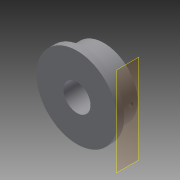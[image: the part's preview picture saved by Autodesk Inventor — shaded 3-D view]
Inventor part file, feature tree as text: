
AUTODESK INVENTOR PART (.ipt)
format: ipt  version: 2015 SP2 (Build 190223200, 223)  size: 109,056 bytes
history: native  units: mm
features: sketch x4, extrude x3, plane x1, hole x1
ambient origin geometry x8: Origin, YZ Plane, XZ Plane, XY Plane, X Axis, Y Axis, Z Axis, Center Point
bodies: Solid1 (feature_tree)
feature tree (9):
  extrude  "Extrusion1"  TaperAngle=0.0deg  [1 undecoded]
  extrude  "Extrusion2"  Depth=10.0mm
  extrude  "Extrusion3"  [1 undecoded]
  plane  "Work Plane1"
  hole  "Hole1"  [1 undecoded]
  sketch  "Sketch1"  dims[d2=0.0mm d5=0.0mm]
  sketch  "Sketch2"  dims[d7=10.0mm d8=0.0mm d9=30.0mm]
  sketch  "Sketch3"  dims[d10=15.0mm]
  sketch  "Sketch4"  dims[d11=3.242mm d12=8.0mm d13=4.0mm d14=2.0mm d15=90.0deg d16=8.0mm d17=20.594885mm]
note: 3 required parameter values undecoded (feature->parameter linkage not recoverable at this tier; creation-order binding heuristic only, values carry confidence <= 0.55)
